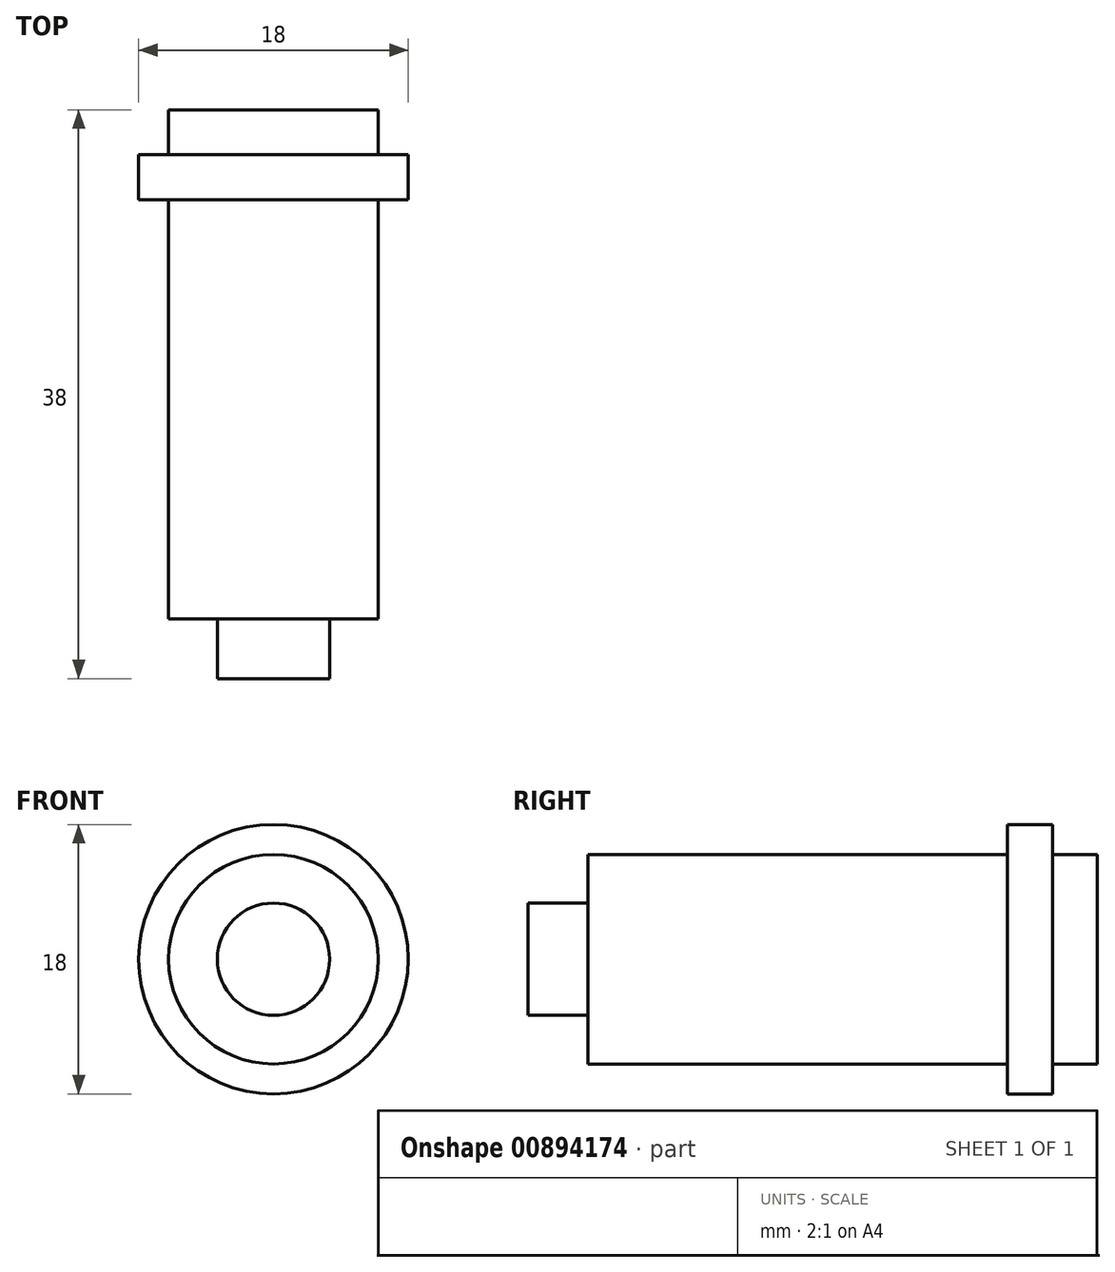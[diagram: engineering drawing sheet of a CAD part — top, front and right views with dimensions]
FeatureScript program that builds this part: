
annotation { "Feature Type Name" : "Feature", "Feature Type Description" : "" }
export const myFeature = defineFeature(function(context is Context, id is Id, definition is map)
    precondition{}
    {
        {
            var Q0;
            Q0=qCreatedBy(makeId("Front.planeOp"),FACE);
            var sketch = newSketch(context, id + "F0", { "sketchPlane" : qUnion([Q0])});
            skCircle(sketch, "E0", {"center": v(0, 0) * mm, "radius": 7 * mm});
            skCircle(sketch, "E1", {"center": v(0, 0) * mm, "radius": 9 * mm});
            skCircle(sketch, "E2", {"center": v(0, 0) * mm, "radius": 3.75 * mm});
            skSolve(sketch);
        }
        {
            var Q0;
            Q0=makeQuery(id+"F0.imprint","IMPRINT",FACE,{"disambiguationData":[TD([[makeQuery(id+"F0.imprint","IMPRINT",EDGE,{"derivedFrom":sQuery(id+"F0.wireOp",EDGE,"E0")}),1.0]])]});
            extrude(context, id + "F1", {"entities" : qUnion([Q0]), "depth" : 31 * mm, "offsetDistance" : 25 * mm});
        }
        {
            var Q0;
            Q0=makeQuery(id+"F0.imprint","IMPRINT",FACE,{"disambiguationData":[TD([[makeQuery(id+"F0.imprint","IMPRINT",EDGE,{"derivedFrom":sQuery(id+"F0.wireOp",EDGE,"E0")}),-1.0]])]});
            extrude(context, id + "F2", {"entities" : qUnion([Q0]), "operationType" : NewBodyOperationType.ADD, "depth" : 3 * mm, "offsetDistance" : 25 * mm});
        }
        {
            var Q0;
            Q0=makeQuery(id+"F0.imprint","IMPRINT",FACE,{"disambiguationData":[TD([[makeQuery(id+"F0.imprint","IMPRINT",EDGE,{"derivedFrom":sQuery(id+"F0.wireOp",EDGE,"E0")}),1.0]])]});
            extrude(context, id + "F3", {"entities" : qUnion([Q0]), "operationType" : NewBodyOperationType.ADD, "oppositeDirection" : true, "depth" : 3 * mm, "offsetDistance" : 25 * mm});
        }
        {
            var Q0;
            Q0=makeQuery(id+"F0.imprint","IMPRINT",FACE,{"disambiguationData":[TD([[makeQuery(id+"F0.imprint","IMPRINT",EDGE,{"derivedFrom":sQuery(id+"F0.wireOp",EDGE,"E2")}),1.0]])]});
            extrude(context, id + "F4", {"entities" : qUnion([Q0]), "operationType" : NewBodyOperationType.ADD, "oppositeDirection" : true, "depth" : 3 * mm, "offsetDistance" : 25 * mm});
        }
        {
            var Q0;
            Q0=makeQuery(id+"F0.imprint","IMPRINT",FACE,{"disambiguationData":[TD([[makeQuery(id+"F0.imprint","IMPRINT",EDGE,{"derivedFrom":sQuery(id+"F0.wireOp",EDGE,"E2")}),1.0]])]});
            extrude(context, id + "F5", {"entities" : qUnion([Q0]), "operationType" : NewBodyOperationType.ADD, "depth" : 35 * mm, "offsetDistance" : 25 * mm});
        }
    });
